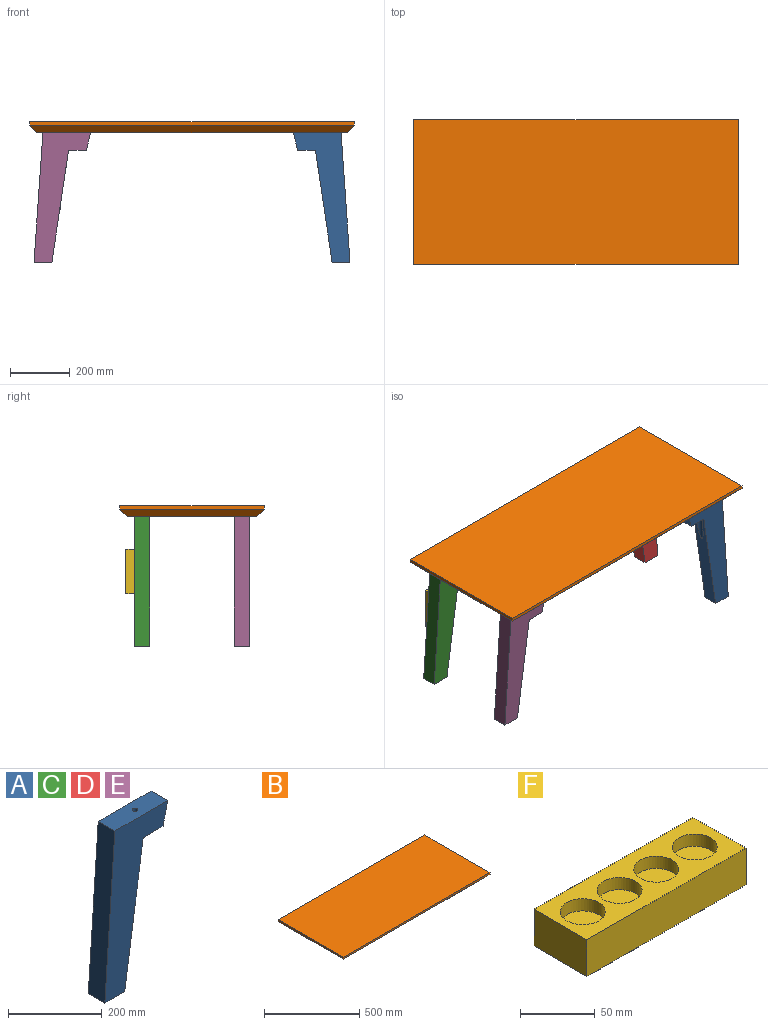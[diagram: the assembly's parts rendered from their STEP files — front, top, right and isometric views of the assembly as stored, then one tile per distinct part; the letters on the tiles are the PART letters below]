
ASSEMBLY  parts=6 mates=5
PART A: 13 faces, bbox 190x50x435 mm
  f0: cylinder r=6mm len=50mm, axis (0,0,-1), area 1885mm2, adj f1,f10
  f1: plane 160x50mm, normal (0,0,1), area 7886.9mm2, adj f0,f2,f6,f7,f8
  f2: plane 435x50mm, normal (-1,0,0.07), area 21801.7mm2, adj f1,f3,f7,f8
  f3: plane 60x50mm, normal (0,0,-1), area 2037.9mm2, adj f2,f4,f7,f8,f11
  f4: plane 375x55.86mm, normal (0.99,0,-0.15), area 16558.2mm2, adj f3,f5,f7,f8,f9
  f5: plane 60x50mm, normal (0,0,-1), area 2646.6mm2, adj f4,f6,f7,f8,f9
  f6: plane 60x50mm, normal (0.97,0,-0.23), area 3082.2mm2, adj f1,f5,f7,f8
  f7: plane 435x190mm, normal (0,-1,0), area 37425mm2, adj f1,f2,f3,f4,f5,f6
  f8: plane 435x190mm, normal (0,1,0), area 37425mm2, adj f1,f2,f3,f4,f5,f6
  f9: cylinder r=15mm len=111.04mm, axis (0,0,1), area 3963.3mm2, adj f4,f5,f10
  f10: plane 30x30mm, normal (0,0,-1), area 593.8mm2, adj f0,f9
  f11: cylinder r=17.5mm len=35mm, axis (0,0,-1), area 219.9mm2, adj f3,f12
  f12: plane 35x35mm, normal (0,0,-1), area 962.1mm2, adj f11
PART B: 10 faces, bbox 1090x485x36 mm
  f0: plane 485x11mm, normal (1,0,0), area 5335mm2, adj f1,f3,f4,f6
  f1: plane 1090x11mm, normal (0,1,0), area 11990mm2, adj f0,f2,f4,f7
  f2: plane 485x11mm, normal (-1,0,0), area 5335mm2, adj f1,f3,f4,f9
  f3: plane 1090x11mm, normal (0,-1,0), area 11990mm2, adj f0,f2,f4,f8
  f4: plane 1090x485mm, normal (0,0,1), area 528650mm2, adj f0,f1,f2,f3
  f5: plane 1040x435mm, normal (0,0,-1), area 452400mm2, adj f6,f7,f8,f9
  f6: plane 485x25mm, normal (0.71,0,-0.71), area 16263.5mm2, adj f0,f5,f7,f8
  f7: plane 1090x25mm, normal (0,0.71,-0.71), area 37653.4mm2, adj f1,f5,f6,f9
  f8: plane 1090x25mm, normal (0,-0.71,-0.71), area 37653.4mm2, adj f3,f5,f6,f9
  f9: plane 485x25mm, normal (-0.71,0,-0.71), area 16263.5mm2, adj f2,f5,f7,f8
PART C: same geometry as A
PART D: same geometry as A
PART E: same geometry as A
PART F: 14 faces, bbox 150x50x30 mm
  f0: plane 50x30mm, normal (-1,0,0), area 1500mm2, adj f1,f3,f4,f5
  f1: plane 150x30mm, normal (0,-1,0), area 4500mm2, adj f0,f2,f4,f5
  f2: plane 50x30mm, normal (1,0,0), area 1500mm2, adj f1,f3,f4,f5
  f3: plane 150x30mm, normal (0,1,0), area 4500mm2, adj f0,f2,f4,f5
  f4: plane 150x50mm, normal (0,0,1), area 4672.6mm2, adj f0,f1,f2,f3,f6,f8,f10,f12
  f5: plane 150x50mm, normal (0,0,-1), area 7500mm2, adj f0,f1,f2,f3
  f6: cylinder r=15mm len=30mm, axis (0,0,1), area 942.5mm2, adj f4,f7
  f7: plane 30x30mm, normal (0,0,1), area 706.9mm2, adj f6
  f8: cylinder r=15mm len=30mm, axis (0,0,1), area 942.5mm2, adj f4,f9
  f9: plane 30x30mm, normal (0,0,1), area 706.9mm2, adj f8
  f10: cylinder r=15mm len=30mm, axis (0,0,1), area 942.5mm2, adj f4,f11
  f11: plane 30x30mm, normal (0,0,1), area 706.9mm2, adj f10
  f12: cylinder r=15mm len=30mm, axis (0,0,1), area 942.5mm2, adj f4,f13
  f13: plane 30x30mm, normal (0,0,1), area 706.9mm2, adj f12
PLACE A rot(axis=(0,0,1),180deg) t=(709.25,-44.59,-178.3)mm
PLACE B t=(209.25,147.91,-178.3)mm
PLACE C t=(-290.75,340.41,-178.3)mm
PLACE D rot(axis=(0,0,1),180deg) t=(709.25,290.41,-178.3)mm
PLACE E t=(-290.75,5.41,-178.3)mm
PLACE F rot(axis=(-0.58,0.58,0.58),120deg) t=(-236.7,340.41,-345.97)mm
MATE fastened F.f5 <-> C.f8  axis (0,-1,0) through (-255.61,340.41,-362.28)mm
MATE fastened D.f9 <-> B.f5  axis (0,0,1) through (623.39,315.41,-178.3)mm
MATE fastened A.f9 <-> B.f5  axis (0,0,1) through (623.39,-19.59,-178.3)mm
MATE fastened B.f5 <-> E.f9  axis (0,0,1) through (-204.88,-19.59,-178.3)mm
MATE fastened B.f5 <-> C.f9  axis (0,0,1) through (-204.88,315.41,-178.3)mm
